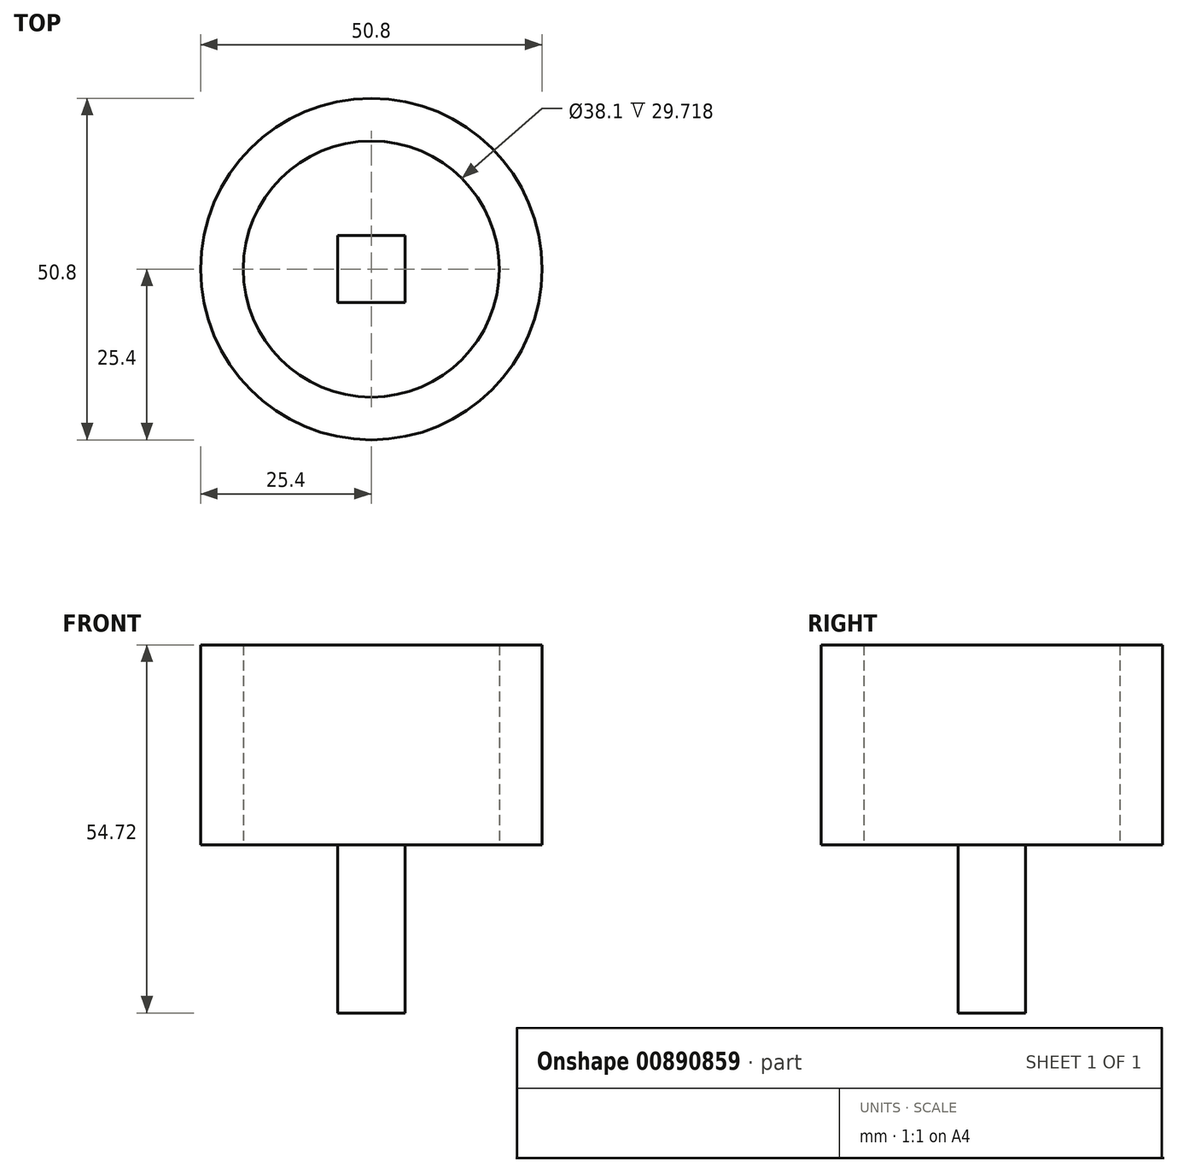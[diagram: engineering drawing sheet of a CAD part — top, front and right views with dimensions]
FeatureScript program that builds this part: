
annotation { "Feature Type Name" : "Feature", "Feature Type Description" : "" }
export const myFeature = defineFeature(function(context is Context, id is Id, definition is map)
    precondition{}
    {
        {
            var Q0;
            Q0=qCreatedBy(makeId("Top.planeOp"),FACE);
            var sketch = newSketch(context, id + "F0", { "sketchPlane" : qUnion([Q0])});
            skLineSegment(sketch, "E0.bottom", {"start": v(5, 5) * mm, "end": v(-5, 5) * mm});
            skLineSegment(sketch, "E0.top", {"start": v(5, -5) * mm, "end": v(-5, -5) * mm});
            skLineSegment(sketch, "E0.left", {"start": v(5, 5) * mm, "end": v(5, -5) * mm});
            skLineSegment(sketch, "E0.right", {"start": v(-5, 5) * mm, "end": v(-5, -5) * mm});
            skPoint(sketch, "E0.middle", {"position": v(0, 0) * mm});
            skSolve(sketch);
        }
        {
            var Q0;
            Q0 = qSketchRegion(id + "F0", true);
            extrude(context, id + "F1", {"entities" : qUnion([Q0]), "depth" : 25 * mm, "offsetDistance" : 25.4 * mm});
        }
        {
            var Q0;
            Q0=makeQuery(id+"F1.opExtrude","CAP_FACE",FACE,{"disambiguationData":[OSD([sQuery(id+"F0.wireOp",EDGE,"E0.bottom"),sQuery(id+"F0.wireOp",EDGE,"E0.top"),sQuery(id+"F0.wireOp",EDGE,"E0.left"),sQuery(id+"F0.wireOp",EDGE,"E0.right")])],"isStart":false});
            var sketch = newSketch(context, id + "F2", { "sketchPlane" : qUnion([Q0])});
            skCircle(sketch, "E1", {"center": v(0, 0) * mm, "radius": 25.4 * mm});
            skCircle(sketch, "E2", {"center": v(0, 0) * mm, "radius": 19.05 * mm});
            skSolve(sketch);
        }
        {
            var Q0;
            Q0=makeQuery(id+"F2.imprint","IMPRINT",FACE,{"disambiguationData":[TD([[makeQuery(id+"F2.imprint","IMPRINT",EDGE,{"derivedFrom":sQuery(id+"F2.wireOp",EDGE,"E1")}),1.0]])]});
            extrude(context, id + "F3", {"entities" : qUnion([Q0]), "depth" : 29.72 * mm, "offsetDistance" : 25.4 * mm});
        }
    });
